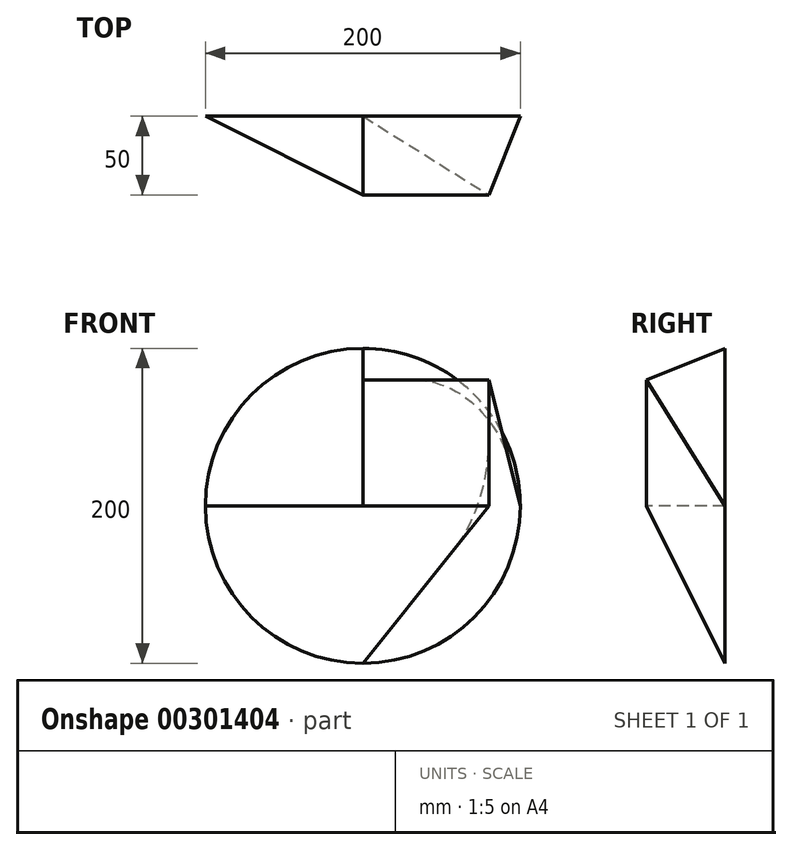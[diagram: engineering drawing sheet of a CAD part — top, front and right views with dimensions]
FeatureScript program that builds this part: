
annotation { "Feature Type Name" : "Feature", "Feature Type Description" : "" }
export const myFeature = defineFeature(function(context is Context, id is Id, definition is map)
    precondition{}
    {
        {
            var Q0;
            Q0=qCreatedBy(makeId("Front.planeOp"),FACE);
            var sketch = newSketch(context, id + "F0", { "sketchPlane" : qUnion([Q0])});
            skCircle(sketch, "E0", {"center": v(0, 0) * mm, "radius": 100 * mm});
            skSolve(sketch);
        }
        {
            var Q0;
            Q0=qCreatedBy(makeId("Front.planeOp"),FACE);
            cPlane(context, id + "F1", {"entities" : qUnion([Q0]), "cplaneType" : CPlaneType.OFFSET, "offset" : 50 * mm, "width" : 150 * mm, "height" : 150 * mm});
        }
        {
            var Q0;
            Q0=qCreatedBy(id+"F1.planeOp",FACE);
            var sketch = newSketch(context, id + "F2", { "sketchPlane" : qUnion([Q0])});
            skLineSegment(sketch, "E1.bottom", {"start": v(0, 0) * mm, "end": v(80, 0) * mm});
            skLineSegment(sketch, "E1.top", {"start": v(0, 80) * mm, "end": v(80, 80) * mm});
            skLineSegment(sketch, "E1.left", {"start": v(0, 0) * mm, "end": v(0, 80) * mm});
            skLineSegment(sketch, "E1.right", {"start": v(80, 0) * mm, "end": v(80, 80) * mm});
            skSolve(sketch);
        }
        {
            var Q0;
            Q0=makeQuery(id+"F0.imprint","IMPRINT",FACE,{"disambiguationData":[TD([[makeQuery(id+"F0.imprint","IMPRINT",EDGE,{"derivedFrom":sQuery(id+"F0.wireOp",EDGE,"E0")}),1.0]])]});
            var Q1;
            Q1=makeQuery(id+"F2.imprint","IMPRINT",FACE,{"disambiguationData":[TD([[makeQuery(id+"F2.imprint","IMPRINT",EDGE,{"derivedFrom":sQuery(id+"F2.wireOp",EDGE,"E1.bottom")}),1.0]])]});
            loft(context, id + "F3", {"sheetProfilesArray" : [{ "sheetProfileEntities" : qUnion([Q0]) }, { "sheetProfileEntities" : qUnion([Q1]) }]});
        }
    });
